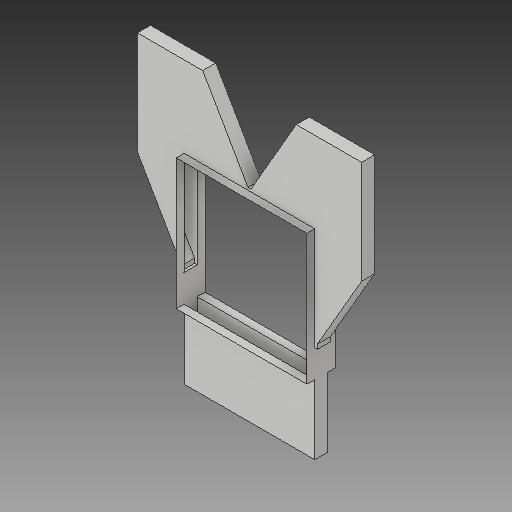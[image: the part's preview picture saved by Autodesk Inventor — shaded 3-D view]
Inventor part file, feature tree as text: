
AUTODESK INVENTOR PART (.ipt)
format: ipt  version: 2017 (Build 210142000, 142)  size: 151,040 bytes
history: native  units: in
note: dims shown in document units (in); Inventor stores cm internally (conversion verified against a paired STEP export)
features: other x4, delete_face x1, sketch x1
ambient origin geometry x8: Origin, YZ Plane, XZ Plane, XY Plane, X Axis, Y Axis, Z Axis, Center Point
bodies: Solid1 (feature_tree)
feature tree (6):
  other  "end door frame (100).ipt"
  delete_face  "Delete Face1"
  sketch  "Sketch2"  dims[d0=0.0354in]
  other  "connection for doors"
  other  "rame of door::end door frame (100).ipt"
  other  "TaggingFeature1"
